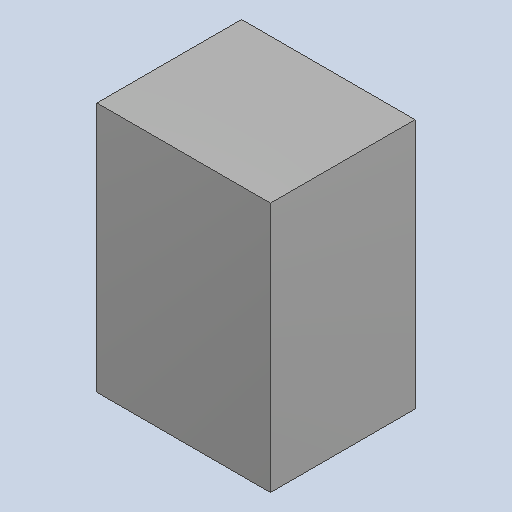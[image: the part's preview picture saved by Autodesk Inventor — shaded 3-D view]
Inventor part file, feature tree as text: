
AUTODESK INVENTOR PART (.ipt)
format: ipt  version: 2023.4 (Build 274418000, 418)  size: 82,944 bytes
history: native  units: mm
features: extrude x1
ambient origin geometry x8: Origin, YZ Plane, XZ Plane, XY Plane, X Axis, Y Axis, Z Axis, Center Point
bodies: Solid1 (feature_tree)
feature tree (1):
  extrude  "Extruded"  [1 undecoded]
note: 1 required parameter value undecoded (feature->parameter linkage not recoverable at this tier; creation-order binding heuristic only, values carry confidence <= 0.55)
